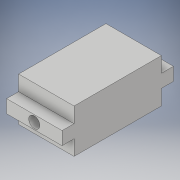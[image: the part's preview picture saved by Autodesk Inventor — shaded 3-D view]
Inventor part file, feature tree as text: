
AUTODESK INVENTOR PART (.ipt)
format: ipt  version: 2017 (Build 210142000, 142)  size: 120,832 bytes
history: native  units: in
note: dims shown in document units (in); Inventor stores cm internally (conversion verified against a paired STEP export)
features: projected_geometry x3, extrude x2, sketch x2
ambient origin geometry x8: Origin, YZ Plane, XZ Plane, XY Plane, X Axis, Y Axis, Z Axis, Center Point
bodies: Solid1 (feature_tree)
feature tree (7):
  extrude  "Extrusion1"  Depth=1.576in
  extrude  "Extrusion2"  Depth=0.236in
  sketch  "Sketch1"  dims[d0=0.7874in d1=1.576in]
  sketch  "Sketch2"  dims[d2=0.217in d3=0.236in d4=0.217in d5=0.2757in d6=0.2757in d7=0.236in d8=1.0in d9=0.0in d10=0.2in d11=5.0in d12=0.0in]
  projected_geometry  "Projected Loop1"
  projected_geometry  "Projected Loop2"
  projected_geometry  "Projected Loop3"
